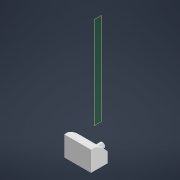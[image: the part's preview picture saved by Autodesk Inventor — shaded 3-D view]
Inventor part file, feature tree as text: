
AUTODESK INVENTOR PART (.ipt)
format: ipt  version: 2021 (Build 250183000, 183)  size: 91,136 bytes
history: native  units: mm
features: other x4, plane x2, reference x2, extrude x1, sketch x1
ambient origin geometry x8: Origin, YZ Plane, XZ Plane, XY Plane, X Axis, Y Axis, Z Axis, Center Point
bodies: Body1 (feature_tree)
feature tree (10):
  plane  "Work Plane1"
  plane  "Work Plane2"
  extrude  "Extrusion3"  [1 undecoded]
  sketch  "Sketch3"  dims[d17=12.0mm d18=0.0mm]
  reference  "Reference5"
  reference  "Reference6"
  other  "Assembly1"
  other  "ilmbt_3d_v1"
  other  "knucle_MIR1:1"
  other  "base_:1"
note: 1 required parameter value undecoded (feature->parameter linkage not recoverable at this tier; creation-order binding heuristic only, values carry confidence <= 0.55)
